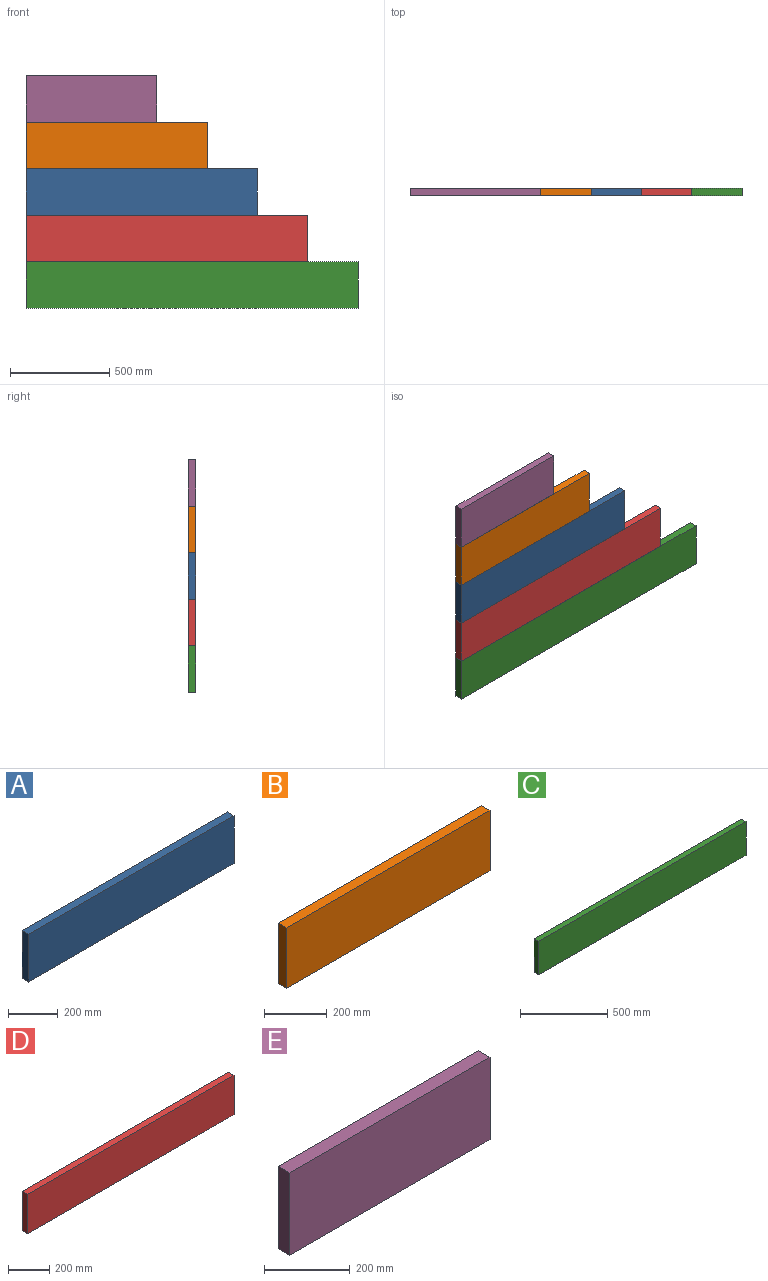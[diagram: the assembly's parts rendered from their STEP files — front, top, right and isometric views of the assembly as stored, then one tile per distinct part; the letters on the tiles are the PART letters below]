
ASSEMBLY  parts=5 mates=12
PART A: 6 faces, bbox 1168.4x38.1x235 mm
  f0: plane 1168.4x38.1mm, normal (0,0,1), area 44516mm2, adj f1,f3,f4,f5
  f1: plane 234.95x38.1mm, normal (-1,0,0), area 8951.6mm2, adj f0,f2,f4,f5
  f2: plane 1168.4x38.1mm, normal (0,0,-1), area 44516mm2, adj f1,f3,f4,f5
  f3: plane 234.95x38.1mm, normal (1,0,0), area 8951.6mm2, adj f0,f2,f4,f5
  f4: plane 1168.4x234.95mm, normal (0,-1,0), area 274515.6mm2, adj f0,f1,f2,f3
  f5: plane 1168.4x234.95mm, normal (0,1,0), area 274515.6mm2, adj f0,f1,f2,f3
PART B: 6 faces, bbox 914.4x38.1x235 mm
  f0: plane 914.4x38.1mm, normal (0,0,1), area 34838.6mm2, adj f1,f3,f4,f5
  f1: plane 234.95x38.1mm, normal (-1,0,0), area 8951.6mm2, adj f0,f2,f4,f5
  f2: plane 914.4x38.1mm, normal (0,0,-1), area 34838.6mm2, adj f1,f3,f4,f5
  f3: plane 234.95x38.1mm, normal (1,0,0), area 8951.6mm2, adj f0,f2,f4,f5
  f4: plane 914.4x234.95mm, normal (0,-1,0), area 214838.3mm2, adj f0,f1,f2,f3
  f5: plane 914.4x234.95mm, normal (0,1,0), area 214838.3mm2, adj f0,f1,f2,f3
PART C: 6 faces, bbox 1676.4x38.1x235 mm
  f0: plane 1676.4x38.1mm, normal (0,0,1), area 63870.8mm2, adj f1,f3,f4,f5
  f1: plane 234.95x38.1mm, normal (-1,0,0), area 8951.6mm2, adj f0,f2,f4,f5
  f2: plane 1676.4x38.1mm, normal (0,0,-1), area 63870.8mm2, adj f1,f3,f4,f5
  f3: plane 234.95x38.1mm, normal (1,0,0), area 8951.6mm2, adj f0,f2,f4,f5
  f4: plane 1676.4x234.95mm, normal (0,-1,0), area 393870.2mm2, adj f0,f1,f2,f3
  f5: plane 1676.4x234.95mm, normal (0,1,0), area 393870.2mm2, adj f0,f1,f2,f3
PART D: 6 faces, bbox 1422.4x38.1x235 mm
  f0: plane 1422.4x38.1mm, normal (0,0,1), area 54193.4mm2, adj f1,f3,f4,f5
  f1: plane 234.95x38.1mm, normal (-1,0,0), area 8951.6mm2, adj f0,f2,f4,f5
  f2: plane 1422.4x38.1mm, normal (0,0,-1), area 54193.4mm2, adj f1,f3,f4,f5
  f3: plane 234.95x38.1mm, normal (1,0,0), area 8951.6mm2, adj f0,f2,f4,f5
  f4: plane 1422.4x234.95mm, normal (0,-1,0), area 334192.9mm2, adj f0,f1,f2,f3
  f5: plane 1422.4x234.95mm, normal (0,1,0), area 334192.9mm2, adj f0,f1,f2,f3
PART E: 6 faces, bbox 660.4x38.1x235 mm
  f0: plane 660.4x38.1mm, normal (0,0,1), area 25161.2mm2, adj f1,f3,f4,f5
  f1: plane 234.95x38.1mm, normal (-1,0,0), area 8951.6mm2, adj f0,f2,f4,f5
  f2: plane 660.4x38.1mm, normal (0,0,-1), area 25161.2mm2, adj f1,f3,f4,f5
  f3: plane 234.95x38.1mm, normal (1,0,0), area 8951.6mm2, adj f0,f2,f4,f5
  f4: plane 660.4x234.95mm, normal (0,-1,0), area 155161mm2, adj f0,f1,f2,f3
  f5: plane 660.4x234.95mm, normal (0,1,0), area 155161mm2, adj f0,f1,f2,f3
PLACE A t=(388.74,-690.69,2708.57)mm
PLACE B t=(388.74,-690.69,2943.52)mm
PLACE C t=(388.74,-690.69,2238.67)mm
PLACE D t=(388.74,-690.69,2473.62)mm
PLACE E t=(388.74,-690.69,3178.47)mm
MATE planar C.f0 <-> D.f2  axis (0,0,1) through (1226.94,-709.74,2473.62)mm
MATE planar A.f0 <-> B.f2  axis (0,0,1) through (972.94,-709.74,2943.52)mm
MATE planar E.f1 <-> B.f1  axis (-1,0,0) through (388.74,-709.74,3295.94)mm
MATE planar A.f1 <-> D.f1  axis (-1,0,0) through (388.74,-709.74,2826.04)mm
MATE planar B.f4 <-> C.f4  axis (0,-1,0) through (845.94,-728.79,3060.99)mm
MATE planar C.f4 <-> D.f4  axis (0,-1,0) through (1226.94,-728.79,2356.14)mm
MATE planar E.f4 <-> C.f4  axis (0,-1,0) through (718.94,-728.79,3295.94)mm
MATE planar B.f1 <-> A.f1  axis (-1,0,0) through (388.74,-709.74,3060.99)mm
MATE planar B.f0 <-> E.f2  axis (0,0,1) through (845.94,-709.74,3178.47)mm
MATE planar A.f4 <-> C.f4  axis (0,-1,0) through (972.94,-728.79,2826.04)mm
MATE planar C.f1 <-> D.f1  axis (-1,0,0) through (388.74,-709.74,2473.62)mm
MATE planar D.f0 <-> A.f2  axis (0,0,1) through (1099.94,-709.74,2708.57)mm
